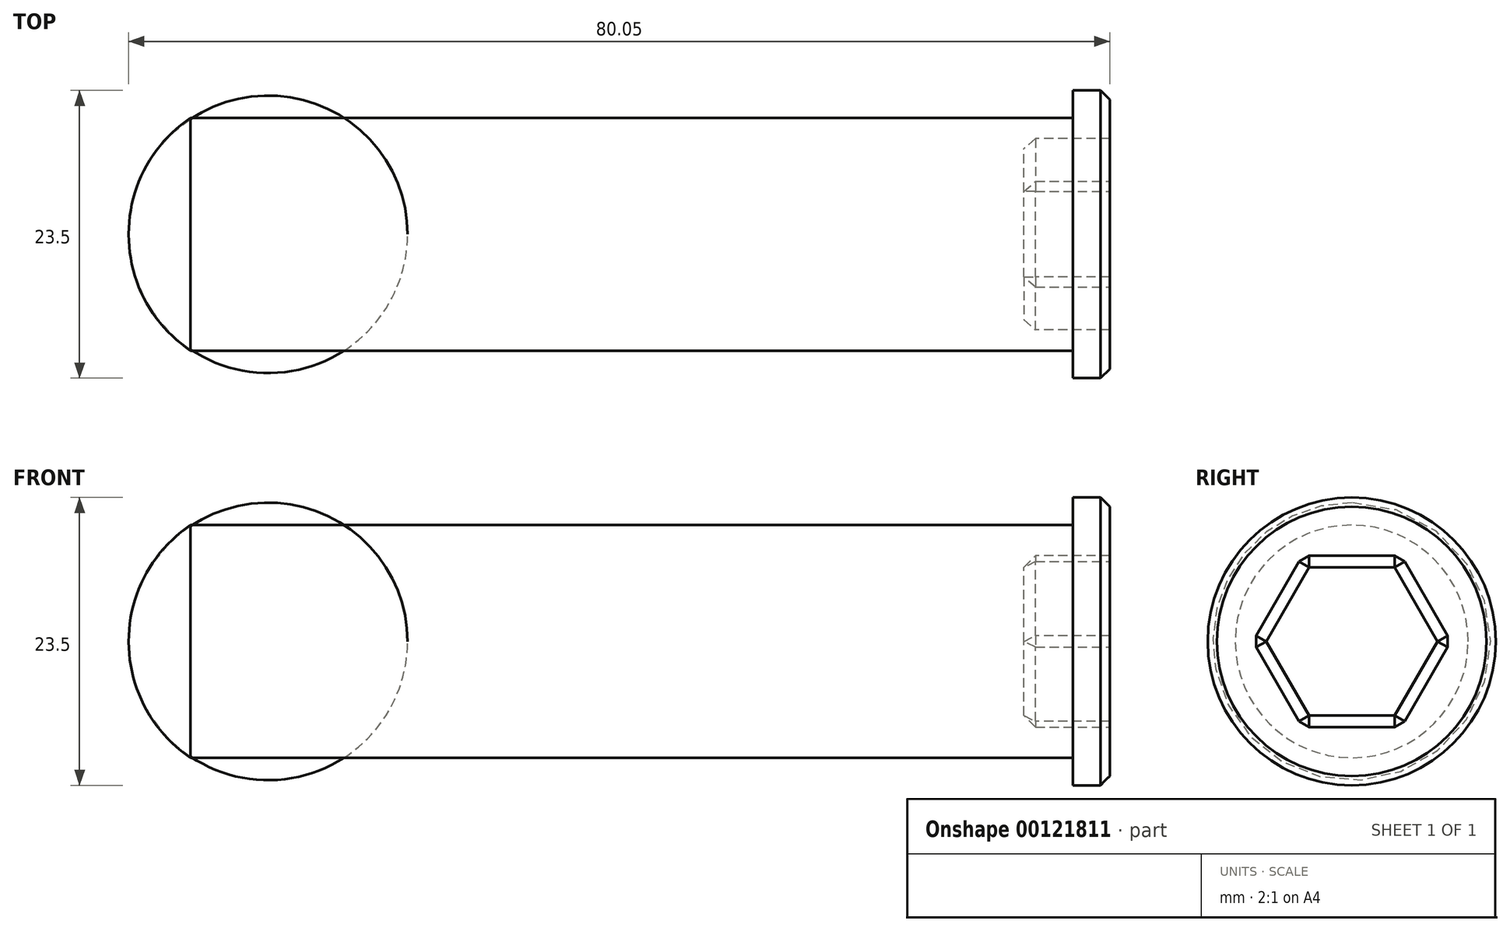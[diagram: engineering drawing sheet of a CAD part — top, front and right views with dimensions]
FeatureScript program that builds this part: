
annotation { "Feature Type Name" : "Feature", "Feature Type Description" : "" }
export const myFeature = defineFeature(function(context is Context, id is Id, definition is map)
    precondition{}
    {
        {
            var Q0;
            Q0=qCreatedBy(makeId("Front.planeOp"),FACE);
            var sketch = newSketch(context, id + "F0", { "sketchPlane" : qUnion([Q0])});
            skLineSegment(sketch, "E0", {"start": v(0, 0) * mm, "end": v(0, 9.5) * mm});
            skLineSegment(sketch, "E1", {"start": v(0, 9.5) * mm, "end": v(-75, 9.5) * mm});
            skLineSegment(sketch, "E2", {"start": v(0, 0) * mm, "end": v(-76.5, 0) * mm});
            skLineSegment(sketch, "E3", {"start": v(-76.5, 0) * mm, "end": v(-80.05, 0) * mm});
            skArc(sketch, "E4", {"start": v(-75, 9.5) * mm, "mid": v(-78.72, 5.38) * mm, "end": v(-80.05, 0) * mm});
            skSolve(sketch);
        }
        {
            var Q0;
            Q0=makeQuery(id+"F0.imprint","IMPRINT",FACE,{"disambiguationData":[TD([[makeQuery(id+"F0.imprint","IMPRINT",EDGE,{"derivedFrom":sQuery(id+"F0.wireOp",EDGE,"E0")}),1.0]])]});
            var Q1;
            Q1=sQuery(id+"F0.wireOp",EDGE,"E2");
            revolve(context, id + "F1", {"entities" : qUnion([Q0]), "axis" : qUnion([Q1]), "revolveType" : RevolveType.FULL});
        }
        {
            var Q0;
            Q0=makeQuery(id+"F1.opRevolve","SWEPT_FACE",FACE,{"disambiguationData":[OSD([sQuery(id+"F0.wireOp",EDGE,"E0")])]});
            var sketch = newSketch(context, id + "F2", { "sketchPlane" : qUnion([Q0])});
            skCircle(sketch, "E5", {"center": v(0, 0) * mm, "radius": 11.75 * mm});
            skSolve(sketch);
        }
        {
            var Q0;
            Q0 = qSketchRegion(id + "F2", true);
            extrude(context, id + "F3", {"entities" : qUnion([Q0]), "operationType" : NewBodyOperationType.ADD, "oppositeDirection" : true, "depth" : 3 * mm});
        }
        {
            var Q0;
            Q0=makeQuery(id+"F3.boolean.opBoolean","MERGE",FACE,{"derivedFrom":[makeQuery(id+"F1.opRevolve","SWEPT_FACE",FACE,{"disambiguationData":[OSD([sQuery(id+"F0.wireOp",EDGE,"E0")])]}),makeQuery(id+"F3.opExtrude","CAP_FACE",FACE,{"disambiguationData":[OSD([sQuery(id+"F2.wireOp",EDGE,"E5")])],"isStart":true})]});
            var sketch = newSketch(context, id + "F4", { "sketchPlane" : qUnion([Q0])});
            skCircle(sketch, "E6.cCircle", {"center": v(0, 0) * mm, "radius": 7 * mm, "construction": true});
            skLineSegment(sketch, "E6.0", {"start": v(-4.04, 7) * mm, "end": v(4.04, 7) * mm});
            skLineSegment(sketch, "E6.1", {"start": v(4.04, 7) * mm, "end": v(8.08, 0) * mm});
            skLineSegment(sketch, "E6.2", {"start": v(8.08, 0) * mm, "end": v(4.04, -7) * mm});
            skLineSegment(sketch, "E6.3", {"start": v(4.04, -7) * mm, "end": v(-4.04, -7) * mm});
            skLineSegment(sketch, "E6.4", {"start": v(-4.04, -7) * mm, "end": v(-8.08, 0) * mm});
            skLineSegment(sketch, "E6.5", {"start": v(-8.08, 0) * mm, "end": v(-4.04, 7) * mm});
            skPoint(sketch, "E6.0.midPoint", {"position": v(0, 7) * mm});
            skSolve(sketch);
        }
        {
            var Q0;
            Q0 = qSketchRegion(id + "F4", true);
            extrude(context, id + "F5", {"entities" : qUnion([Q0]), "operationType" : NewBodyOperationType.REMOVE, "oppositeDirection" : true, "depth" : 7 * mm});
        }
        {
            var Q0;
            Q0=makeQuery(id+"F3.opExtrude","CAP_EDGE",EDGE,{"disambiguationData":[OSD([sQuery(id+"F2.wireOp",EDGE,"E5")])],"isStart":true});
            chamfer(context, id + "F6", {"entities" : qUnion([Q0]), "width" : .75 * mm, "tangentPropagation" : true});
        }
        {
            var Q0;
            Q0=makeQuery(id+"F5.boolean.opBoolean","COPY",EDGE,{"derivedFrom":makeQuery(id+"F5.opExtrude","CAP_EDGE",EDGE,{"disambiguationData":[OSD([sQuery(id+"F4.wireOp",EDGE,"E6.3")])],"isStart":true})});
            var Q1;
            Q1=makeQuery(id+"F5.boolean.opBoolean","COPY",EDGE,{"derivedFrom":makeQuery(id+"F5.opExtrude","CAP_EDGE",EDGE,{"disambiguationData":[OSD([sQuery(id+"F4.wireOp",EDGE,"E6.2")])],"isStart":true})});
            var Q2;
            Q2=makeQuery(id+"F5.boolean.opBoolean","COPY",EDGE,{"derivedFrom":makeQuery(id+"F5.opExtrude","CAP_EDGE",EDGE,{"disambiguationData":[OSD([sQuery(id+"F4.wireOp",EDGE,"E6.1")])],"isStart":true})});
            var Q3;
            Q3=makeQuery(id+"F5.boolean.opBoolean","COPY",EDGE,{"derivedFrom":makeQuery(id+"F5.opExtrude","CAP_EDGE",EDGE,{"disambiguationData":[OSD([sQuery(id+"F4.wireOp",EDGE,"E6.0")])],"isStart":true})});
            var Q4;
            Q4=makeQuery(id+"F5.boolean.opBoolean","COPY",EDGE,{"derivedFrom":makeQuery(id+"F5.opExtrude","CAP_EDGE",EDGE,{"disambiguationData":[OSD([sQuery(id+"F4.wireOp",EDGE,"E6.5")])],"isStart":true})});
            var Q5;
            Q5=makeQuery(id+"F5.boolean.opBoolean","COPY",EDGE,{"derivedFrom":makeQuery(id+"F5.opExtrude","CAP_EDGE",EDGE,{"disambiguationData":[OSD([sQuery(id+"F4.wireOp",EDGE,"E6.4")])],"isStart":true})});
            var Q6;
            Q6=makeQuery(id+"F5.boolean.opBoolean","COPY",EDGE,{"derivedFrom":makeQuery(id+"F5.opExtrude","SWEPT_EDGE",EDGE,{"disambiguationData":[OSD([sQuery(id+"F4.wireOp",EDGE,"E6.1"),sQuery(id+"F4.wireOp",EDGE,"E6.2")])]})});
            var Q7;
            Q7=makeQuery(id+"F5.boolean.opBoolean","COPY",EDGE,{"derivedFrom":makeQuery(id+"F5.opExtrude","SWEPT_EDGE",EDGE,{"disambiguationData":[OSD([sQuery(id+"F4.wireOp",EDGE,"E6.0"),sQuery(id+"F4.wireOp",EDGE,"E6.1")])]})});
            var Q8;
            Q8=makeQuery(id+"F5.boolean.opBoolean","COPY",EDGE,{"derivedFrom":makeQuery(id+"F5.opExtrude","SWEPT_EDGE",EDGE,{"disambiguationData":[OSD([sQuery(id+"F4.wireOp",EDGE,"E6.0"),sQuery(id+"F4.wireOp",EDGE,"E6.5")])]})});
            var Q9;
            Q9=makeQuery(id+"F5.boolean.opBoolean","COPY",EDGE,{"derivedFrom":makeQuery(id+"F5.opExtrude","SWEPT_EDGE",EDGE,{"disambiguationData":[OSD([sQuery(id+"F4.wireOp",EDGE,"E6.4"),sQuery(id+"F4.wireOp",EDGE,"E6.5")])]})});
            var Q10;
            Q10=makeQuery(id+"F5.boolean.opBoolean","COPY",EDGE,{"derivedFrom":makeQuery(id+"F5.opExtrude","SWEPT_EDGE",EDGE,{"disambiguationData":[OSD([sQuery(id+"F4.wireOp",EDGE,"E6.3"),sQuery(id+"F4.wireOp",EDGE,"E6.4")])]})});
            var Q11;
            Q11=makeQuery(id+"F5.boolean.opBoolean","COPY",EDGE,{"derivedFrom":makeQuery(id+"F5.opExtrude","CAP_EDGE",EDGE,{"disambiguationData":[OSD([sQuery(id+"F4.wireOp",EDGE,"E6.3")])],"isStart":false})});
            var Q12;
            Q12=makeQuery(id+"F5.boolean.opBoolean","COPY",EDGE,{"derivedFrom":makeQuery(id+"F5.opExtrude","CAP_EDGE",EDGE,{"disambiguationData":[OSD([sQuery(id+"F4.wireOp",EDGE,"E6.4")])],"isStart":false})});
            var Q13;
            Q13=makeQuery(id+"F5.boolean.opBoolean","COPY",EDGE,{"derivedFrom":makeQuery(id+"F5.opExtrude","CAP_EDGE",EDGE,{"disambiguationData":[OSD([sQuery(id+"F4.wireOp",EDGE,"E6.5")])],"isStart":false})});
            var Q14;
            Q14=makeQuery(id+"F5.boolean.opBoolean","COPY",EDGE,{"derivedFrom":makeQuery(id+"F5.opExtrude","CAP_EDGE",EDGE,{"disambiguationData":[OSD([sQuery(id+"F4.wireOp",EDGE,"E6.0")])],"isStart":false})});
            var Q15;
            Q15=makeQuery(id+"F5.boolean.opBoolean","COPY",EDGE,{"derivedFrom":makeQuery(id+"F5.opExtrude","CAP_EDGE",EDGE,{"disambiguationData":[OSD([sQuery(id+"F4.wireOp",EDGE,"E6.1")])],"isStart":false})});
            var Q16;
            Q16=makeQuery(id+"F5.boolean.opBoolean","COPY",EDGE,{"derivedFrom":makeQuery(id+"F5.opExtrude","CAP_EDGE",EDGE,{"disambiguationData":[OSD([sQuery(id+"F4.wireOp",EDGE,"E6.2")])],"isStart":false})});
            var Q17;
            Q17=makeQuery(id+"F5.boolean.opBoolean","COPY",EDGE,{"derivedFrom":makeQuery(id+"F5.opExtrude","SWEPT_EDGE",EDGE,{"disambiguationData":[OSD([sQuery(id+"F4.wireOp",EDGE,"E6.2"),sQuery(id+"F4.wireOp",EDGE,"E6.3")])]})});
            chamfer(context, id + "F7", {"entities" : qUnion([Q0, Q1, Q2, Q3, Q4, Q5, Q6, Q7, Q8, Q9, Q10, Q11, Q12, Q13, Q14, Q15, Q16, Q17]), "width" : .95 * mm, "tangentPropagation" : true});
        }
    });
